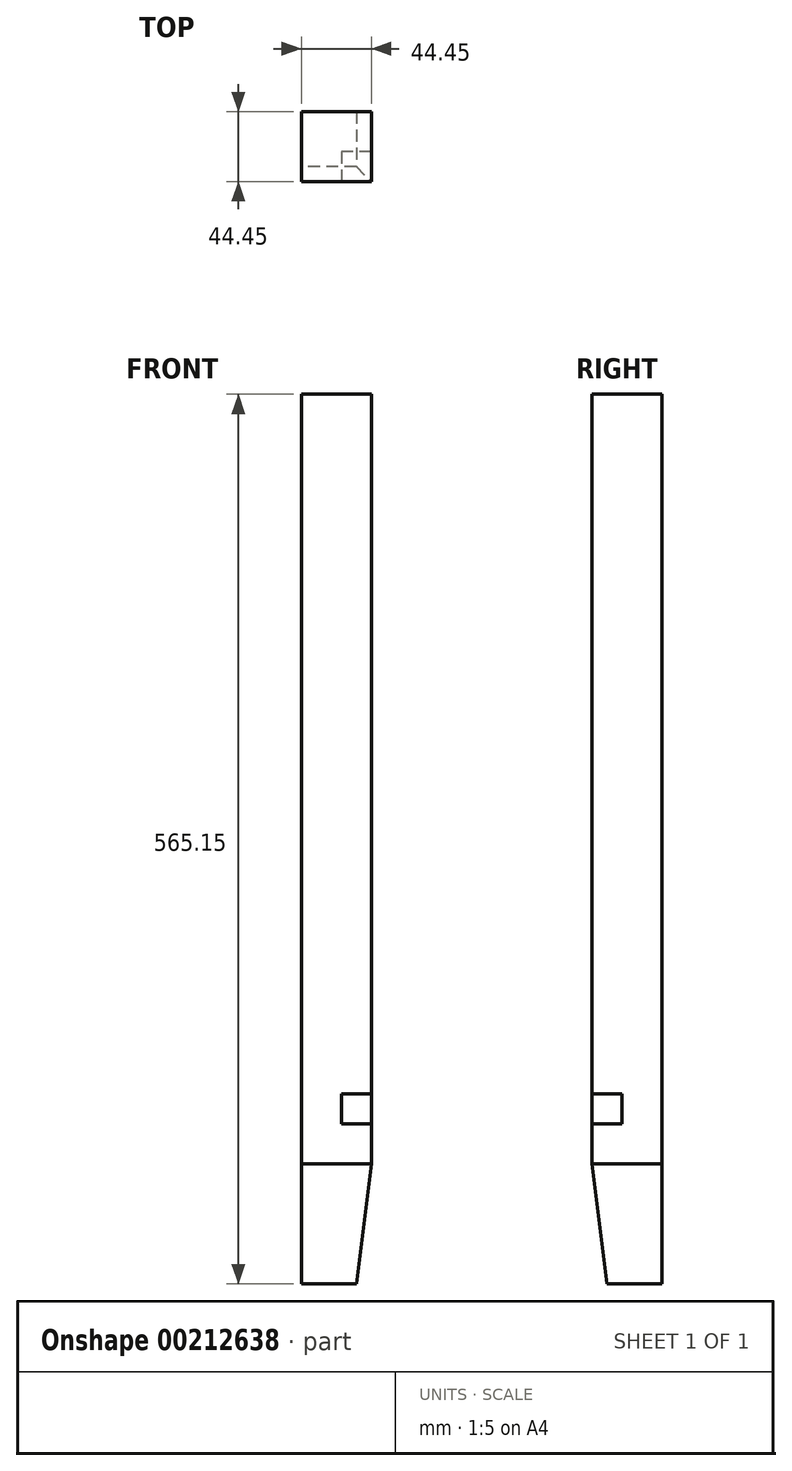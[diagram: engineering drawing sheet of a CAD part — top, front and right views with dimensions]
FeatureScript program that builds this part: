
annotation { "Feature Type Name" : "Feature", "Feature Type Description" : "" }
export const myFeature = defineFeature(function(context is Context, id is Id, definition is map)
    precondition{}
    {
        {
            var Q0;
            Q0=qCreatedBy(makeId("Top.planeOp"),FACE);
            var sketch = newSketch(context, id + "F0", { "sketchPlane" : qUnion([Q0])});
            skLineSegment(sketch, "E0.bottom", {"start": v(-44.45, 44.45) * mm, "end": v(0, 44.45) * mm});
            skLineSegment(sketch, "E0.top", {"start": v(-44.45, 0) * mm, "end": v(0, 0) * mm});
            skLineSegment(sketch, "E0.left", {"start": v(-44.45, 44.45) * mm, "end": v(-44.45, 0) * mm});
            skLineSegment(sketch, "E0.right", {"start": v(0, 44.45) * mm, "end": v(0, 0) * mm});
            skSolve(sketch);
        }
        {
            var Q0;
            Q0 = qSketchRegion(id + "F0", true);
            extrude(context, id + "F1", {"entities" : qUnion([Q0]), "oppositeDirection" : true, "depth" : 565.15 * mm});
        }
        {
            var Q0;
            Q0=makeQuery(id+"F1.opExtrude","SWEPT_FACE",FACE,{"disambiguationData":[OSD([sQuery(id+"F0.wireOp",EDGE,"E0.top")])]});
            var sketch = newSketch(context, id + "F2", { "sketchPlane" : qUnion([Q0])});
            skLineSegment(sketch, "E1", {"start": v(0, -565.15) * mm, "end": v(0, -488.95) * mm});
            skLineSegment(sketch, "E2", {"start": v(0, -488.95) * mm, "end": v(-9.53, -565.15) * mm});
            skLineSegment(sketch, "E3", {"start": v(-9.53, -565.15) * mm, "end": v(0, -565.15) * mm});
            skSolve(sketch);
        }
        {
            var Q0;
            Q0=makeQuery(id+"F2.imprint","IMPRINT",FACE,{"disambiguationData":[TD([[makeQuery(id+"F2.imprint","IMPRINT",EDGE,{"derivedFrom":sQuery(id+"F2.wireOp",EDGE,"E1")}),1.0]])]});
            extrude(context, id + "F3", {"entities" : qUnion([Q0]), "operationType" : NewBodyOperationType.REMOVE, "endBound" : BoundingType.UP_TO_NEXT, "oppositeDirection" : true, "depth" : 25.4 * mm});
        }
        {
            var Q0;
            Q0=makeQuery(id+"F1.opExtrude","SWEPT_FACE",FACE,{"disambiguationData":[OSD([sQuery(id+"F0.wireOp",EDGE,"E0.left")])]});
            var sketch = newSketch(context, id + "F4", { "sketchPlane" : qUnion([Q0])});
            skLineSegment(sketch, "E4", {"start": v(0, -488.95) * mm, "end": v(-9.53, -565.15) * mm});
            skLineSegment(sketch, "E5", {"start": v(-9.53, -565.15) * mm, "end": v(0, -565.15) * mm});
            skLineSegment(sketch, "E6", {"start": v(0, -565.15) * mm, "end": v(0, -488.95) * mm});
            skSolve(sketch);
        }
        {
            var Q0;
            Q0 = qSketchRegion(id + "F4", true);
            extrude(context, id + "F5", {"entities" : qUnion([Q0]), "operationType" : NewBodyOperationType.REMOVE, "endBound" : BoundingType.UP_TO_NEXT, "oppositeDirection" : true, "depth" : 25.4 * mm});
        }
        {
            var Q0;
            Q0=makeQuery(id+"F1.opExtrude","SWEPT_FACE",FACE,{"disambiguationData":[OSD([sQuery(id+"F0.wireOp",EDGE,"E0.top")])]});
            var sketch = newSketch(context, id + "F6", { "sketchPlane" : qUnion([Q0])});
            skLineSegment(sketch, "E7.bottom", {"start": v(0, -463.55) * mm, "end": v(-19.05, -463.55) * mm});
            skLineSegment(sketch, "E7.top", {"start": v(0, -444.5) * mm, "end": v(-19.05, -444.5) * mm});
            skLineSegment(sketch, "E7.left", {"start": v(0, -463.55) * mm, "end": v(0, -444.5) * mm});
            skLineSegment(sketch, "E7.right", {"start": v(-19.05, -463.55) * mm, "end": v(-19.05, -444.5) * mm});
            skSolve(sketch);
        }
        {
            var Q0;
            Q0=makeQuery(id+"F6.imprint","IMPRINT",FACE,{"disambiguationData":[TD([[makeQuery(id+"F6.imprint","IMPRINT",EDGE,{"derivedFrom":sQuery(id+"F6.wireOp",EDGE,"E7.bottom")}),-1.0]])]});
            extrude(context, id + "F7", {"entities" : qUnion([Q0]), "operationType" : NewBodyOperationType.REMOVE, "oppositeDirection" : true, "depth" : 19.05 * mm});
        }
    });
